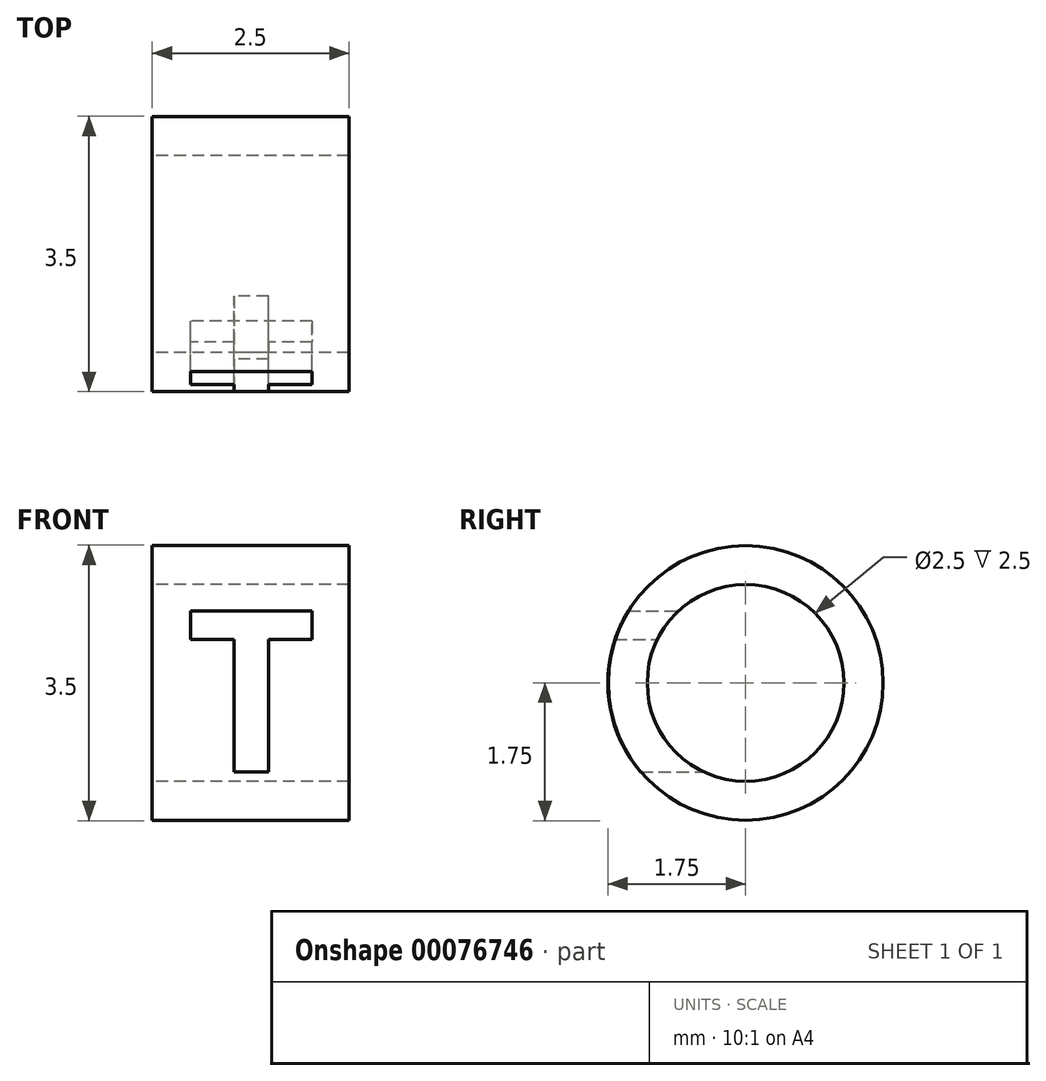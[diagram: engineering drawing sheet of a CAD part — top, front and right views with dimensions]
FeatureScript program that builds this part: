
annotation { "Feature Type Name" : "Feature", "Feature Type Description" : "" }
export const myFeature = defineFeature(function(context is Context, id is Id, definition is map)
    precondition{}
    {
        {
            var Q0;
            Q0=qCreatedBy(makeId("Right.planeOp"),FACE);
            var sketch = newSketch(context, id + "F0", { "sketchPlane" : qUnion([Q0])});
            skCircle(sketch, "E0", {"center": v(0, 0) * mm, "radius": 1.25 * mm});
            skCircle(sketch, "E1", {"center": v(0, 0) * mm, "radius": 1.75 * mm});
            skSolve(sketch);
        }
        {
            var Q0;
            Q0=makeQuery(id+"F0.imprint","IMPRINT",FACE,{"disambiguationData":[TD([[makeQuery(id+"F0.imprint","IMPRINT",EDGE,{"derivedFrom":sQuery(id+"F0.wireOp",EDGE,"E0")}),-1.0]])]});
            var Q1;
            Q1=makeQuery(id+"F0.imprint","IMPRINT",FACE,{"disambiguationData":[TD([[makeQuery(id+"F0.imprint","IMPRINT",EDGE,{"derivedFrom":sQuery(id+"F0.wireOp",EDGE,"E1")}),1.0]])]});
            extrude(context, id + "F1", {"entities" : qUnion([Q0, Q1]), "depth" : 2.5 * mm});
        }
        {
            var Q0;
            Q0=qCreatedBy(makeId("Front.planeOp"),FACE);
            var sketch = newSketch(context, id + "F2", { "sketchPlane" : qUnion([Q0])});
            skText(sketch, "E2", { "text": "T\n", "fontName": "OpenSans-Bold.ttf"});
            const initialGuessF2  = {"E2": [0.00043, -0.00113, 1, 0, 0.00206]};
            skSetInitialGuess(sketch, initialGuessF2);
            skSolve(sketch);
        }
        {
            var Q0;
            Q0 = qSketchRegion(id + "F2", true);
            var Q1;
            Q1 = qConstructionFilter(qBodyType(qCreatedBy(id + "F2" ,EDGE), BodyType.WIRE), ConstructionObject.NO);
            var Q2;
            Q2=makeQuery(id+"F1.opExtrude","SWEPT_FACE",FACE,{"disambiguationData":[OSD([sQuery(id+"F0.wireOp",EDGE,"E1")])]});
            var Q3;
            Q3=makeQuery(id+"F1.opExtrude","SWEPT_BODY",BODY,{"disambiguationData":[OSD([sQuery(id+"F0.wireOp",EDGE,"E0"),sQuery(id+"F0.wireOp",EDGE,"E1")])]});
            var Q4;
            Q4=sQuery(id+"F0.wireOp",VERTEX,"27635d6e-dcd6-4653-b727-4819003c0945");
            extrude(context, id + "F3", {"entities" : qUnion([Q0]), "operationType" : NewBodyOperationType.INTERSECT, "surfaceEntities" : qUnion([Q1]), "endBound" : BoundingType.UP_TO_SURFACE, "endBoundEntityFace" : qUnion([Q2]), "endBoundEntityBody" : qUnion([Q3]), "endBoundEntityVertex" : qUnion([Q4]), "depth" : 25 * mm});
        }
        {
            var Q0;
            Q0=makeQuery(id+"F0.imprint","IMPRINT",FACE,{"disambiguationData":[TD([[makeQuery(id+"F0.imprint","IMPRINT",EDGE,{"derivedFrom":sQuery(id+"F0.wireOp",EDGE,"E0")}),-1.0]])]});
            extrude(context, id + "F4", {"entities" : qUnion([Q0]), "depth" : 2.5 * mm});
        }
    });
